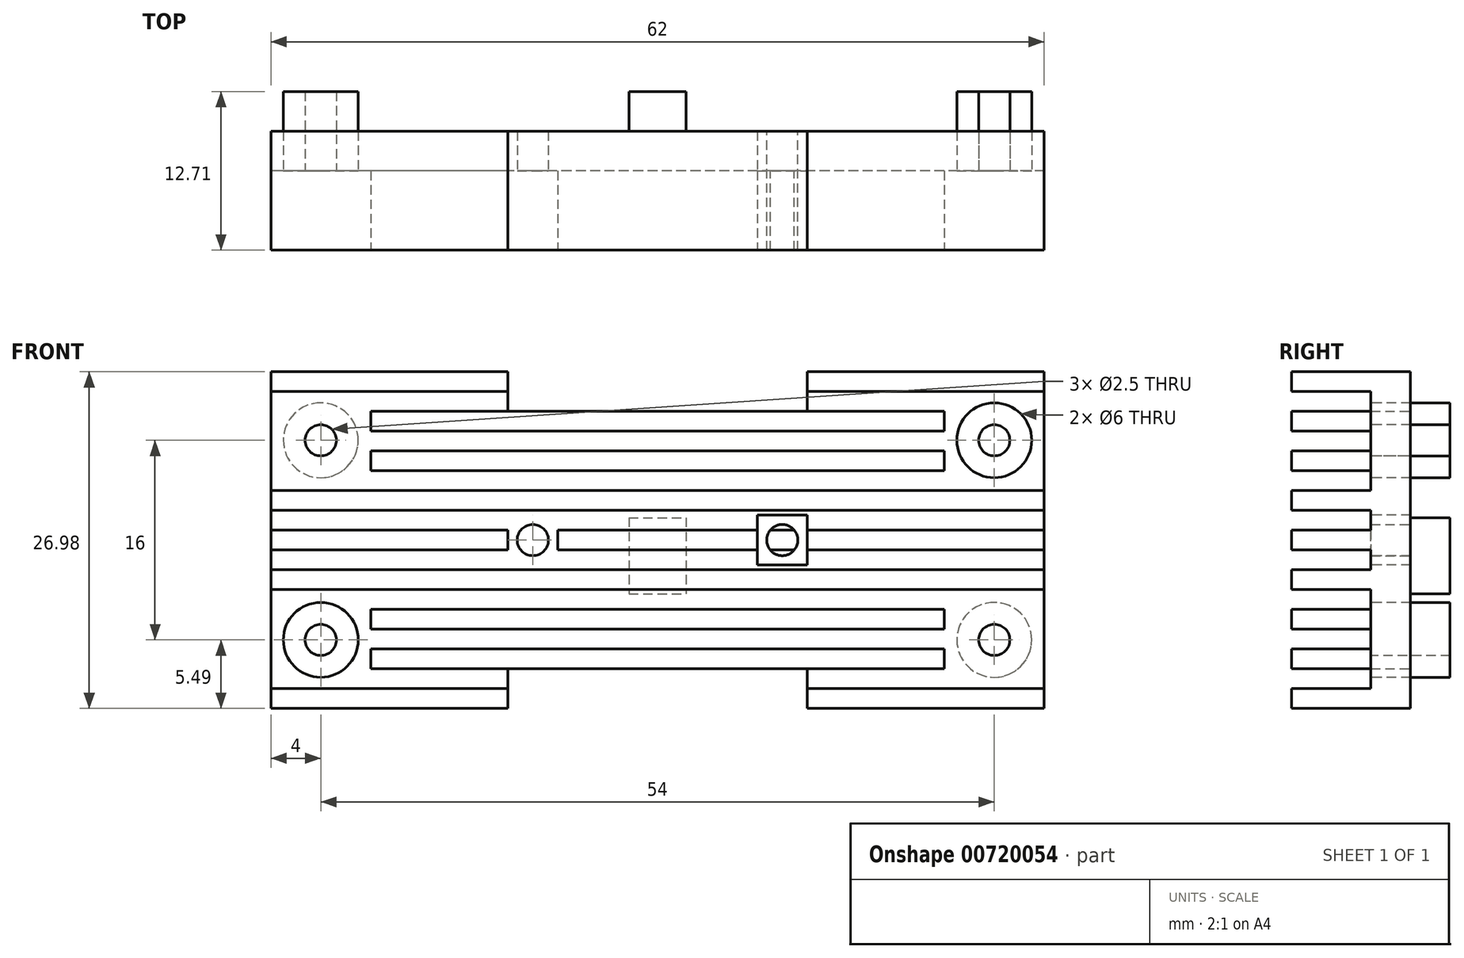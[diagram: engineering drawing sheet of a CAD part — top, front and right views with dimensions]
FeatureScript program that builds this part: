
annotation { "Feature Type Name" : "Feature", "Feature Type Description" : "" }
export const myFeature = defineFeature(function(context is Context, id is Id, definition is map)
    precondition{}
    {
        {
            var Q0;
            Q0=qCreatedBy(makeId("Front.planeOp"),FACE);
            var sketch = newSketch(context, id + "F0", { "sketchPlane" : qUnion([Q0])});
            skLineSegment(sketch, "E0", {"start": v(0, 0) * mm, "end": v(-31, 0) * mm, "construction": true});
            skLineSegment(sketch, "E1", {"start": v(-31, 0) * mm, "end": v(-31, 13.5) * mm, "construction": true});
            skLineSegment(sketch, "E2.bottom", {"start": v(-31, 13.5) * mm, "end": v(31, 13.5) * mm});
            skLineSegment(sketch, "E2.top", {"start": v(-31, -13.5) * mm, "end": v(31, -13.5) * mm});
            skLineSegment(sketch, "E2.left", {"start": v(-31, 13.5) * mm, "end": v(-31, -13.5) * mm});
            skLineSegment(sketch, "E2.right", {"start": v(31, 13.5) * mm, "end": v(31, -13.5) * mm});
            skPoint(sketch, "E2.middle", {"position": v(0, 0) * mm});
            skLineSegment(sketch, "E3", {"start": v(0, 0) * mm, "end": v(12, 0) * mm, "construction": true});
            skLineSegment(sketch, "E4", {"start": v(12, 0) * mm, "end": v(12, 10.32) * mm, "construction": true});
            skLineSegment(sketch, "E5", {"start": v(12, 10.32) * mm, "end": v(12, 13.5) * mm});
            skLineSegment(sketch, "E6", {"start": v(12, 10.32) * mm, "end": v(0, 10.32) * mm});
            skLineSegment(sketch, "E7.MirrorCS", {"start": v(-12, 10.32) * mm, "end": v(-12, 13.5) * mm});
            skLineSegment(sketch, "E8.MirrorCS", {"start": v(-12, 10.32) * mm, "end": v(0, 10.32) * mm});
            skLineSegment(sketch, "E9.MirrorCS", {"start": v(-12, -10.32) * mm, "end": v(-12, -13.5) * mm});
            skLineSegment(sketch, "E10.MirrorCS", {"start": v(-12, -10.32) * mm, "end": v(0, -10.32) * mm});
            skLineSegment(sketch, "E11.MirrorCS", {"start": v(12, -10.32) * mm, "end": v(12, -13.5) * mm});
            skLineSegment(sketch, "E12.MirrorCS", {"start": v(12, -10.32) * mm, "end": v(0, -10.32) * mm});
            skSolve(sketch);
        }
        {
            var Q0;
            Q0=makeQuery(id+"F0.imprint","IMPRINT",FACE,{"disambiguationData":[TD([[makeQuery(id+"F0.imprint","IMPRINT",EDGE,{"derivedFrom":sQuery(id+"F0.wireOp",EDGE,"E2.bottom")}),-1.0]])]});
            extrude(context, id + "F1", {"entities" : qUnion([Q0]), "depth" : 9.53 * mm, "offsetDistance" : 25 * mm});
        }
        {
            var Q0;
            Q0=makeQuery(id+"F1.opExtrude","CAP_FACE",FACE,{"disambiguationData":[OSD([sQuery(id+"F0.wireOp",EDGE,"E2.bottom"),sQuery(id+"F0.wireOp",EDGE,"E2.top"),sQuery(id+"F0.wireOp",EDGE,"E2.left"),sQuery(id+"F0.wireOp",EDGE,"E2.right")])],"isStart":false});
            var sketch = newSketch(context, id + "F2", { "sketchPlane" : qUnion([Q0])});
            skLineSegment(sketch, "E13.bottom", {"start": v(-31, 0.8) * mm, "end": v(31, 0.8) * mm});
            skLineSegment(sketch, "E13.top", {"start": v(-31, -0.8) * mm, "end": v(31, -0.8) * mm});
            skLineSegment(sketch, "E13.left", {"start": v(-31, 0.8) * mm, "end": v(-31, -0.8) * mm});
            skLineSegment(sketch, "E13.right", {"start": v(31, 0.8) * mm, "end": v(31, -0.8) * mm});
            skPoint(sketch, "E13.middle", {"position": v(0, 0) * mm});
            skLineSegment(sketch, "E14.0.1.0", {"start": v(-31, 3.97) * mm, "end": v(31, 3.97) * mm});
            skLineSegment(sketch, "E14.0.1.1", {"start": v(-31, 3.97) * mm, "end": v(-31, 2.38) * mm});
            skLineSegment(sketch, "E14.0.1.2", {"start": v(-31, 2.38) * mm, "end": v(31, 2.38) * mm});
            skLineSegment(sketch, "E14.0.1.3", {"start": v(31, 3.97) * mm, "end": v(31, 2.38) * mm});
            skLineSegment(sketch, "E14.0.2.0", {"start": v(-31, 7.14) * mm, "end": v(31, 7.14) * mm});
            skLineSegment(sketch, "E14.0.2.1", {"start": v(-31, 7.14) * mm, "end": v(-31, 5.56) * mm});
            skLineSegment(sketch, "E14.0.2.2", {"start": v(-31, 5.56) * mm, "end": v(31, 5.56) * mm});
            skLineSegment(sketch, "E14.0.2.3", {"start": v(31, 7.14) * mm, "end": v(31, 5.56) * mm});
            skLineSegment(sketch, "E14.0.3.0", {"start": v(-31, 10.32) * mm, "end": v(31, 10.32) * mm});
            skLineSegment(sketch, "E14.0.3.1", {"start": v(-31, 10.32) * mm, "end": v(-31, 8.73) * mm});
            skLineSegment(sketch, "E14.0.3.2", {"start": v(-31, 8.73) * mm, "end": v(31, 8.73) * mm});
            skLineSegment(sketch, "E14.0.3.3", {"start": v(31, 10.32) * mm, "end": v(31, 8.73) * mm});
            skLineSegment(sketch, "E14.0.4.0", {"start": v(-31, 13.5) * mm, "end": v(31, 13.5) * mm});
            skLineSegment(sketch, "E14.0.4.1", {"start": v(-31, 13.5) * mm, "end": v(-31, 11.9) * mm});
            skLineSegment(sketch, "E14.0.4.2", {"start": v(-31, 11.9) * mm, "end": v(31, 11.9) * mm});
            skLineSegment(sketch, "E14.0.4.3", {"start": v(31, 13.5) * mm, "end": v(31, 11.9) * mm});
            skLineSegment(sketch, "E14.direction1", {"start": v(-31, 0.8) * mm, "end": v(-6, 0.8) * mm, "construction": true});
            skLineSegment(sketch, "E14.direction2", {"start": v(-31, 0.8) * mm, "end": v(-31, 3.97) * mm, "construction": true});
            skLineSegment(sketch, "E15.MirrorCS", {"start": v(-31, -13.5) * mm, "end": v(31, -13.5) * mm});
            skLineSegment(sketch, "E16.MirrorCS", {"start": v(-31, -13.5) * mm, "end": v(-31, -11.9) * mm});
            skLineSegment(sketch, "E17.MirrorCS", {"start": v(-31, -11.9) * mm, "end": v(31, -11.9) * mm});
            skLineSegment(sketch, "E18.MirrorCS", {"start": v(-31, -10.32) * mm, "end": v(31, -10.32) * mm});
            skLineSegment(sketch, "E19.MirrorCS", {"start": v(-31, -10.32) * mm, "end": v(-31, -8.73) * mm});
            skLineSegment(sketch, "E20.MirrorCS", {"start": v(-31, -8.73) * mm, "end": v(31, -8.73) * mm});
            skLineSegment(sketch, "E21.MirrorCS", {"start": v(-31, -7.14) * mm, "end": v(31, -7.14) * mm});
            skLineSegment(sketch, "E22.MirrorCS", {"start": v(-31, -7.14) * mm, "end": v(-31, -5.56) * mm});
            skLineSegment(sketch, "E23.MirrorCS", {"start": v(-31, -5.56) * mm, "end": v(31, -5.56) * mm});
            skLineSegment(sketch, "E24.MirrorCS", {"start": v(-31, -3.97) * mm, "end": v(31, -3.97) * mm});
            skLineSegment(sketch, "E25.MirrorCS", {"start": v(-31, -3.97) * mm, "end": v(-31, -2.38) * mm});
            skLineSegment(sketch, "E26.MirrorCS", {"start": v(-31, -2.38) * mm, "end": v(31, -2.38) * mm});
            skLineSegment(sketch, "E27.MirrorCS", {"start": v(31, -13.5) * mm, "end": v(31, -11.9) * mm});
            skLineSegment(sketch, "E28.MirrorCS", {"start": v(31, -10.32) * mm, "end": v(31, -8.73) * mm});
            skLineSegment(sketch, "E29.MirrorCS", {"start": v(31, -7.14) * mm, "end": v(31, -5.56) * mm});
            skLineSegment(sketch, "E30.MirrorCS", {"start": v(31, -3.97) * mm, "end": v(31, -2.38) * mm});
            skSolve(sketch);
        }
        {
            var Q0;
            Q0=qCreatedBy(makeId("Front.planeOp"),FACE);
            cPlane(context, id + "F3", {"entities" : qUnion([Q0]), "cplaneType" : CPlaneType.OFFSET, "offset" : 3.17 * mm, "width" : 150 * mm, "height" : 150 * mm});
        }
        {
            var Q0;
            {var subQ0=sQuery(id+"F2.wireOp",EDGE,"E14.0.3.0");var subQ3=makeQuery(id+"F1.opExtrude","CAP_EDGE",EDGE,{"disambiguationData":[OSD([sQuery(id+"F0.wireOp",EDGE,"E7.MirrorCS")])],"isStart":false});var subQ4=makeQuery(id+"F2.imprint","INTERSECT",VERTEX,{"derivedFrom":[subQ3,subQ0]});Q0=makeQuery(id+"F2.imprint","IMPRINT",FACE,{"disambiguationData":[TD([[makeQuery(id+"F2.imprint","IMPRINT",EDGE,{"disambiguationData":[TD([[subQ4,-1.0]])],"derivedFrom":subQ3}),1.0]])]});}
            var Q1;
            {var subQ0=sQuery(id+"F2.wireOp",EDGE,"E14.0.3.0");var subQ3=makeQuery(id+"F1.opExtrude","CAP_EDGE",EDGE,{"disambiguationData":[OSD([sQuery(id+"F0.wireOp",EDGE,"E5")])],"isStart":false});var subQ4=makeQuery(id+"F2.imprint","INTERSECT",VERTEX,{"derivedFrom":[subQ3,subQ0]});Q1=makeQuery(id+"F2.imprint","IMPRINT",FACE,{"disambiguationData":[TD([[makeQuery(id+"F2.imprint","IMPRINT",EDGE,{"disambiguationData":[TD([[subQ4,-1.0]])],"derivedFrom":subQ3}),-1.0]])]});}
            var Q2;
            {var subQ0=sQuery(id+"F2.wireOp",EDGE,"E14.0.2.0");Q2=makeQuery(id+"F2.imprint","IMPRINT",FACE,{"disambiguationData":[TD([[makeQuery(id+"F2.imprint","IMPRINT",EDGE,{"derivedFrom":subQ0}),1.0]])]});}
            var Q3;
            {var subQ0=sQuery(id+"F2.wireOp",EDGE,"E14.0.1.0");Q3=makeQuery(id+"F2.imprint","IMPRINT",FACE,{"disambiguationData":[TD([[makeQuery(id+"F2.imprint","IMPRINT",EDGE,{"derivedFrom":subQ0}),1.0]])]});}
            var Q4;
            {var subQ0=sQuery(id+"F2.wireOp",EDGE,"E13.bottom");Q4=makeQuery(id+"F2.imprint","IMPRINT",FACE,{"disambiguationData":[TD([[makeQuery(id+"F2.imprint","IMPRINT",EDGE,{"derivedFrom":subQ0}),1.0]])]});}
            var Q5;
            {var subQ0=sQuery(id+"F2.wireOp",EDGE,"E13.top");Q5=makeQuery(id+"F2.imprint","IMPRINT",FACE,{"disambiguationData":[TD([[makeQuery(id+"F2.imprint","IMPRINT",EDGE,{"derivedFrom":subQ0}),-1.0]])]});}
            var Q6;
            {var subQ0=sQuery(id+"F2.wireOp",EDGE,"E23.MirrorCS");Q6=makeQuery(id+"F2.imprint","IMPRINT",FACE,{"disambiguationData":[TD([[makeQuery(id+"F2.imprint","IMPRINT",EDGE,{"derivedFrom":subQ0}),1.0]])]});}
            var Q7;
            {var subQ0=sQuery(id+"F2.wireOp",EDGE,"E20.MirrorCS");Q7=makeQuery(id+"F2.imprint","IMPRINT",FACE,{"disambiguationData":[TD([[makeQuery(id+"F2.imprint","IMPRINT",EDGE,{"derivedFrom":subQ0}),1.0]])]});}
            var Q8;
            {var subQ0=sQuery(id+"F2.wireOp",EDGE,"E17.MirrorCS");var subQ3=makeQuery(id+"F1.opExtrude","CAP_EDGE",EDGE,{"disambiguationData":[OSD([sQuery(id+"F0.wireOp",EDGE,"E9.MirrorCS")])],"isStart":false});var subQ4=makeQuery(id+"F2.imprint","INTERSECT",VERTEX,{"derivedFrom":[subQ3,subQ0]});Q8=makeQuery(id+"F2.imprint","IMPRINT",FACE,{"disambiguationData":[TD([[makeQuery(id+"F2.imprint","IMPRINT",EDGE,{"disambiguationData":[TD([[subQ4,1.0]])],"derivedFrom":subQ3}),-1.0]])]});}
            var Q9;
            {var subQ0=sQuery(id+"F2.wireOp",EDGE,"E17.MirrorCS");var subQ3=makeQuery(id+"F1.opExtrude","CAP_EDGE",EDGE,{"disambiguationData":[OSD([sQuery(id+"F0.wireOp",EDGE,"E11.MirrorCS")])],"isStart":false});var subQ4=makeQuery(id+"F2.imprint","INTERSECT",VERTEX,{"derivedFrom":[subQ3,subQ0]});Q9=makeQuery(id+"F2.imprint","IMPRINT",FACE,{"disambiguationData":[TD([[makeQuery(id+"F2.imprint","IMPRINT",EDGE,{"disambiguationData":[TD([[subQ4,1.0]])],"derivedFrom":subQ3}),1.0]])]});}
            var Q10;
            Q10=qCreatedBy(id+"F3.planeOp",FACE);
            extrude(context, id + "F4", {"entities" : qUnion([Q0, Q1, Q2, Q3, Q4, Q5, Q6, Q7, Q8, Q9]), "operationType" : NewBodyOperationType.REMOVE, "endBound" : BoundingType.UP_TO_SURFACE, "oppositeDirection" : true, "depth" : 25 * mm, "endBoundEntityFace" : qUnion([Q10]), "offsetDistance" : 25 * mm});
        }
        {
            var Q0;
            Q0=qCreatedBy(id+"F3.planeOp",FACE);
            var sketch = newSketch(context, id + "F5", { "sketchPlane" : qUnion([Q0])});
            skLineSegment(sketch, "E31", {"start": v(0, 0) * mm, "end": v(-27, 0) * mm, "construction": true});
            skLineSegment(sketch, "E32", {"start": v(-27, 0) * mm, "end": v(-27, 8) * mm, "construction": true});
            skCircle(sketch, "E33", {"center": v(-27, 8) * mm, "radius": 1.25 * mm});
            skCircle(sketch, "E34", {"center": v(-27, 8) * mm, "radius": 3 * mm});
            skLineSegment(sketch, "E35.bottom", {"start": v(-23, 11.5) * mm, "end": v(-31, 11.5) * mm});
            skLineSegment(sketch, "E35.top", {"start": v(-23, 4.5) * mm, "end": v(-31, 4.5) * mm});
            skLineSegment(sketch, "E35.left", {"start": v(-23, 11.5) * mm, "end": v(-23, 4.5) * mm});
            skLineSegment(sketch, "E35.right", {"start": v(-31, 11.5) * mm, "end": v(-31, 4.5) * mm});
            skLineSegment(sketch, "E36", {"start": v(0, 0) * mm, "end": v(-2.3, 0) * mm, "construction": true});
            skLineSegment(sketch, "E37", {"start": v(-2.3, 0) * mm, "end": v(-2.3, 1.8) * mm, "construction": true});
            skLineSegment(sketch, "E38", {"start": v(0, 0) * mm, "end": v(2.3, 0) * mm, "construction": true});
            skLineSegment(sketch, "E39", {"start": v(2.3, 0) * mm, "end": v(2.3, -4.3) * mm, "construction": true});
            skLineSegment(sketch, "E40.bottom", {"start": v(-2.3, 1.8) * mm, "end": v(2.3, 1.8) * mm});
            skLineSegment(sketch, "E40.top", {"start": v(-2.3, -4.3) * mm, "end": v(2.3, -4.3) * mm});
            skLineSegment(sketch, "E40.left", {"start": v(-2.3, 1.8) * mm, "end": v(-2.3, -4.3) * mm});
            skLineSegment(sketch, "E40.right", {"start": v(2.3, 1.8) * mm, "end": v(2.3, -4.3) * mm});
            skLineSegment(sketch, "E41", {"start": v(0, 0) * mm, "end": v(-10, 0) * mm, "construction": true});
            skCircle(sketch, "E42", {"center": v(-10, 0) * mm, "radius": 1.25 * mm});
            skLineSegment(sketch, "E43.bottom", {"start": v(-8, 2) * mm, "end": v(-12, 2) * mm});
            skLineSegment(sketch, "E43.top", {"start": v(-8, -2) * mm, "end": v(-12, -2) * mm});
            skLineSegment(sketch, "E43.left", {"start": v(-8, 2) * mm, "end": v(-8, -2) * mm});
            skLineSegment(sketch, "E43.right", {"start": v(-12, 2) * mm, "end": v(-12, -2) * mm});
            skLineSegment(sketch, "E44.MirrorCS", {"start": v(8, 2) * mm, "end": v(8, -2) * mm});
            skLineSegment(sketch, "E45.MirrorCS", {"start": v(8, 2) * mm, "end": v(12, 2) * mm});
            skCircle(sketch, "E46.MirrorC", {"center": v(10, 0) * mm, "radius": 1.25 * mm});
            skLineSegment(sketch, "E47.MirrorCS", {"start": v(8, -2) * mm, "end": v(12, -2) * mm});
            skLineSegment(sketch, "E48.MirrorCS", {"start": v(12, 2) * mm, "end": v(12, -2) * mm});
            skLineSegment(sketch, "E49.MirrorCS", {"start": v(-23, -4.5) * mm, "end": v(-31, -4.5) * mm});
            skCircle(sketch, "E50.MirrorC", {"center": v(-27, -8) * mm, "radius": 1.25 * mm});
            skCircle(sketch, "E51.MirrorC", {"center": v(-27, -8) * mm, "radius": 3 * mm});
            skLineSegment(sketch, "E52.MirrorCS", {"start": v(-31, -11.5) * mm, "end": v(-31, -4.5) * mm});
            skLineSegment(sketch, "E53.MirrorCS", {"start": v(-23, -11.5) * mm, "end": v(-23, -4.5) * mm});
            skLineSegment(sketch, "E54.MirrorCS", {"start": v(-23, -11.5) * mm, "end": v(-31, -11.5) * mm});
            skCircle(sketch, "E55.MirrorC", {"center": v(27, -8) * mm, "radius": 1.25 * mm});
            skCircle(sketch, "E56.MirrorC", {"center": v(27, -8) * mm, "radius": 3 * mm});
            skLineSegment(sketch, "E57.MirrorCS", {"start": v(23, -11.5) * mm, "end": v(31, -11.5) * mm});
            skLineSegment(sketch, "E58.MirrorCS", {"start": v(31, -11.5) * mm, "end": v(31, -4.5) * mm});
            skLineSegment(sketch, "E59.MirrorCS", {"start": v(23, -11.5) * mm, "end": v(23, -4.5) * mm});
            skLineSegment(sketch, "E60.MirrorCS", {"start": v(23, -4.5) * mm, "end": v(31, -4.5) * mm});
            skLineSegment(sketch, "E61.MirrorCS", {"start": v(23, 4.5) * mm, "end": v(31, 4.5) * mm});
            skLineSegment(sketch, "E62.MirrorCS", {"start": v(31, 11.5) * mm, "end": v(31, 4.5) * mm});
            skLineSegment(sketch, "E63.MirrorCS", {"start": v(23, 11.5) * mm, "end": v(23, 4.5) * mm});
            skLineSegment(sketch, "E64.MirrorCS", {"start": v(23, 11.5) * mm, "end": v(31, 11.5) * mm});
            skCircle(sketch, "E65.MirrorC", {"center": v(27, 8) * mm, "radius": 1.25 * mm});
            skCircle(sketch, "E66.MirrorC", {"center": v(27, 8) * mm, "radius": 3 * mm});
            skSolve(sketch);
        }
        {
            var Q0;
            Q0=makeQuery(id+"F1.opExtrude","CAP_FACE",FACE,{"disambiguationData":[OSD([sQuery(id+"F0.wireOp",EDGE,"E2.bottom"),sQuery(id+"F0.wireOp",EDGE,"E2.top"),sQuery(id+"F0.wireOp",EDGE,"E2.left"),sQuery(id+"F0.wireOp",EDGE,"E2.right")])],"isStart":true});
            cPlane(context, id + "F6", {"entities" : qUnion([Q0]), "cplaneType" : CPlaneType.OFFSET, "offset" : 3.17 * mm, "width" : 150 * mm, "height" : 150 * mm});
        }
        {
            var Q0;
            Q0=makeQuery(id+"F5.imprint","IMPRINT",FACE,{"disambiguationData":[TD([[makeQuery(id+"F5.imprint","IMPRINT",EDGE,{"derivedFrom":sQuery(id+"F5.wireOp",EDGE,"E33")}),-1.0]])]});
            var Q1;
            Q1=makeQuery(id+"F5.imprint","IMPRINT",FACE,{"disambiguationData":[TD([[makeQuery(id+"F5.imprint","IMPRINT",EDGE,{"derivedFrom":sQuery(id+"F5.wireOp",EDGE,"E50.MirrorC")}),1.0]])]});
            var Q2;
            Q2=makeQuery(id+"F5.imprint","IMPRINT",FACE,{"disambiguationData":[TD([[makeQuery(id+"F5.imprint","IMPRINT",EDGE,{"derivedFrom":sQuery(id+"F5.wireOp",EDGE,"E65.MirrorC")}),1.0]])]});
            var Q3;
            Q3=makeQuery(id+"F5.imprint","IMPRINT",FACE,{"disambiguationData":[TD([[makeQuery(id+"F5.imprint","IMPRINT",EDGE,{"derivedFrom":sQuery(id+"F5.wireOp",EDGE,"E55.MirrorC")}),-1.0]])]});
            var Q4;
            Q4=makeQuery(id+"F5.imprint","IMPRINT",FACE,{"disambiguationData":[TD([[makeQuery(id+"F5.imprint","IMPRINT",EDGE,{"derivedFrom":sQuery(id+"F5.wireOp",EDGE,"E40.bottom")}),-1.0]])]});
            var Q5;
            Q5=qCreatedBy(id+"F6.planeOp",FACE);
            extrude(context, id + "F7", {"entities" : qUnion([Q0, Q1, Q2, Q3, Q4]), "operationType" : NewBodyOperationType.ADD, "endBound" : BoundingType.UP_TO_SURFACE, "oppositeDirection" : true, "depth" : 25 * mm, "endBoundEntityFace" : qUnion([Q5]), "offsetDistance" : 25 * mm});
        }
        {
            var Q0;
            Q0=makeQuery(id+"F5.imprint","IMPRINT",FACE,{"disambiguationData":[TD([[makeQuery(id+"F5.imprint","IMPRINT",EDGE,{"derivedFrom":sQuery(id+"F5.wireOp",EDGE,"E34")}),-1.0]])]});
            var Q1;
            Q1=makeQuery(id+"F5.imprint","IMPRINT",FACE,{"disambiguationData":[TD([[makeQuery(id+"F5.imprint","IMPRINT",EDGE,{"derivedFrom":sQuery(id+"F5.wireOp",EDGE,"E33")}),-1.0]])]});
            var Q2;
            Q2=makeQuery(id+"F5.imprint","IMPRINT",FACE,{"disambiguationData":[TD([[makeQuery(id+"F5.imprint","IMPRINT",EDGE,{"derivedFrom":sQuery(id+"F5.wireOp",EDGE,"E33")}),1.0]])]});
            var Q3;
            Q3=makeQuery(id+"F5.imprint","IMPRINT",FACE,{"disambiguationData":[TD([[makeQuery(id+"F5.imprint","IMPRINT",EDGE,{"derivedFrom":sQuery(id+"F5.wireOp",EDGE,"E49.MirrorCS")}),1.0]])]});
            var Q4;
            Q4=makeQuery(id+"F5.imprint","IMPRINT",FACE,{"disambiguationData":[TD([[makeQuery(id+"F5.imprint","IMPRINT",EDGE,{"derivedFrom":sQuery(id+"F5.wireOp",EDGE,"E50.MirrorC")}),1.0]])]});
            var Q5;
            Q5=makeQuery(id+"F5.imprint","IMPRINT",FACE,{"disambiguationData":[TD([[makeQuery(id+"F5.imprint","IMPRINT",EDGE,{"derivedFrom":sQuery(id+"F5.wireOp",EDGE,"E50.MirrorC")}),-1.0]])]});
            var Q6;
            Q6=makeQuery(id+"F5.imprint","IMPRINT",FACE,{"disambiguationData":[TD([[makeQuery(id+"F5.imprint","IMPRINT",EDGE,{"derivedFrom":sQuery(id+"F5.wireOp",EDGE,"E42")}),-1.0]])]});
            var Q7;
            Q7=makeQuery(id+"F5.imprint","IMPRINT",FACE,{"disambiguationData":[TD([[makeQuery(id+"F5.imprint","IMPRINT",EDGE,{"derivedFrom":sQuery(id+"F5.wireOp",EDGE,"E42")}),1.0]])]});
            var Q8;
            Q8=makeQuery(id+"F5.imprint","IMPRINT",FACE,{"disambiguationData":[TD([[makeQuery(id+"F5.imprint","IMPRINT",EDGE,{"derivedFrom":sQuery(id+"F5.wireOp",EDGE,"E61.MirrorCS")}),1.0]])]});
            var Q9;
            Q9=makeQuery(id+"F5.imprint","IMPRINT",FACE,{"disambiguationData":[TD([[makeQuery(id+"F5.imprint","IMPRINT",EDGE,{"derivedFrom":sQuery(id+"F5.wireOp",EDGE,"E65.MirrorC")}),1.0]])]});
            var Q10;
            Q10=makeQuery(id+"F5.imprint","IMPRINT",FACE,{"disambiguationData":[TD([[makeQuery(id+"F5.imprint","IMPRINT",EDGE,{"derivedFrom":sQuery(id+"F5.wireOp",EDGE,"E65.MirrorC")}),-1.0]])]});
            var Q11;
            Q11=makeQuery(id+"F5.imprint","IMPRINT",FACE,{"disambiguationData":[TD([[makeQuery(id+"F5.imprint","IMPRINT",EDGE,{"derivedFrom":sQuery(id+"F5.wireOp",EDGE,"E55.MirrorC")}),1.0]])]});
            var Q12;
            Q12=makeQuery(id+"F5.imprint","IMPRINT",FACE,{"disambiguationData":[TD([[makeQuery(id+"F5.imprint","IMPRINT",EDGE,{"derivedFrom":sQuery(id+"F5.wireOp",EDGE,"E55.MirrorC")}),-1.0]])]});
            var Q13;
            Q13=makeQuery(id+"F5.imprint","IMPRINT",FACE,{"disambiguationData":[TD([[makeQuery(id+"F5.imprint","IMPRINT",EDGE,{"derivedFrom":sQuery(id+"F5.wireOp",EDGE,"E56.MirrorC")}),-1.0]])]});
            var Q14;
            Q14=makeQuery(id+"F5.imprint","IMPRINT",FACE,{"disambiguationData":[TD([[makeQuery(id+"F5.imprint","IMPRINT",EDGE,{"derivedFrom":sQuery(id+"F5.wireOp",EDGE,"E44.MirrorCS")}),1.0]])]});
            var Q15;
            Q15=makeQuery(id+"F5.imprint","IMPRINT",FACE,{"disambiguationData":[TD([[makeQuery(id+"F5.imprint","IMPRINT",EDGE,{"derivedFrom":sQuery(id+"F5.wireOp",EDGE,"E46.MirrorC")}),-1.0]])]});
            extrude(context, id + "F8", {"entities" : qUnion([Q0, Q1, Q2, Q3, Q4, Q5, Q6, Q7, Q8, Q9, Q10, Q11, Q12, Q13, Q14, Q15]), "operationType" : NewBodyOperationType.REMOVE, "endBound" : BoundingType.THROUGH_ALL, "depth" : 25 * mm, "offsetDistance" : 25 * mm});
        }
        {
            var Q0;
            Q0=makeQuery(id+"F5.imprint","IMPRINT",FACE,{"disambiguationData":[TD([[makeQuery(id+"F5.imprint","IMPRINT",EDGE,{"derivedFrom":sQuery(id+"F5.wireOp",EDGE,"E33")}),1.0]])]});
            var Q1;
            Q1=makeQuery(id+"F5.imprint","IMPRINT",FACE,{"disambiguationData":[TD([[makeQuery(id+"F5.imprint","IMPRINT",EDGE,{"derivedFrom":sQuery(id+"F5.wireOp",EDGE,"E50.MirrorC")}),-1.0]])]});
            var Q2;
            Q2=makeQuery(id+"F5.imprint","IMPRINT",FACE,{"disambiguationData":[TD([[makeQuery(id+"F5.imprint","IMPRINT",EDGE,{"derivedFrom":sQuery(id+"F5.wireOp",EDGE,"E65.MirrorC")}),-1.0]])]});
            var Q3;
            Q3=makeQuery(id+"F5.imprint","IMPRINT",FACE,{"disambiguationData":[TD([[makeQuery(id+"F5.imprint","IMPRINT",EDGE,{"derivedFrom":sQuery(id+"F5.wireOp",EDGE,"E55.MirrorC")}),1.0]])]});
            var Q4;
            Q4=makeQuery(id+"F5.imprint","IMPRINT",FACE,{"disambiguationData":[TD([[makeQuery(id+"F5.imprint","IMPRINT",EDGE,{"derivedFrom":sQuery(id+"F5.wireOp",EDGE,"E42")}),1.0]])]});
            var Q5;
            Q5=makeQuery(id+"F5.imprint","IMPRINT",FACE,{"disambiguationData":[TD([[makeQuery(id+"F5.imprint","IMPRINT",EDGE,{"derivedFrom":sQuery(id+"F5.wireOp",EDGE,"E46.MirrorC")}),-1.0]])]});
            extrude(context, id + "F9", {"entities" : qUnion([Q0, Q1, Q2, Q3, Q4, Q5]), "operationType" : NewBodyOperationType.REMOVE, "endBound" : BoundingType.THROUGH_ALL, "oppositeDirection" : true, "depth" : 25 * mm, "offsetDistance" : 25 * mm});
        }
    });
